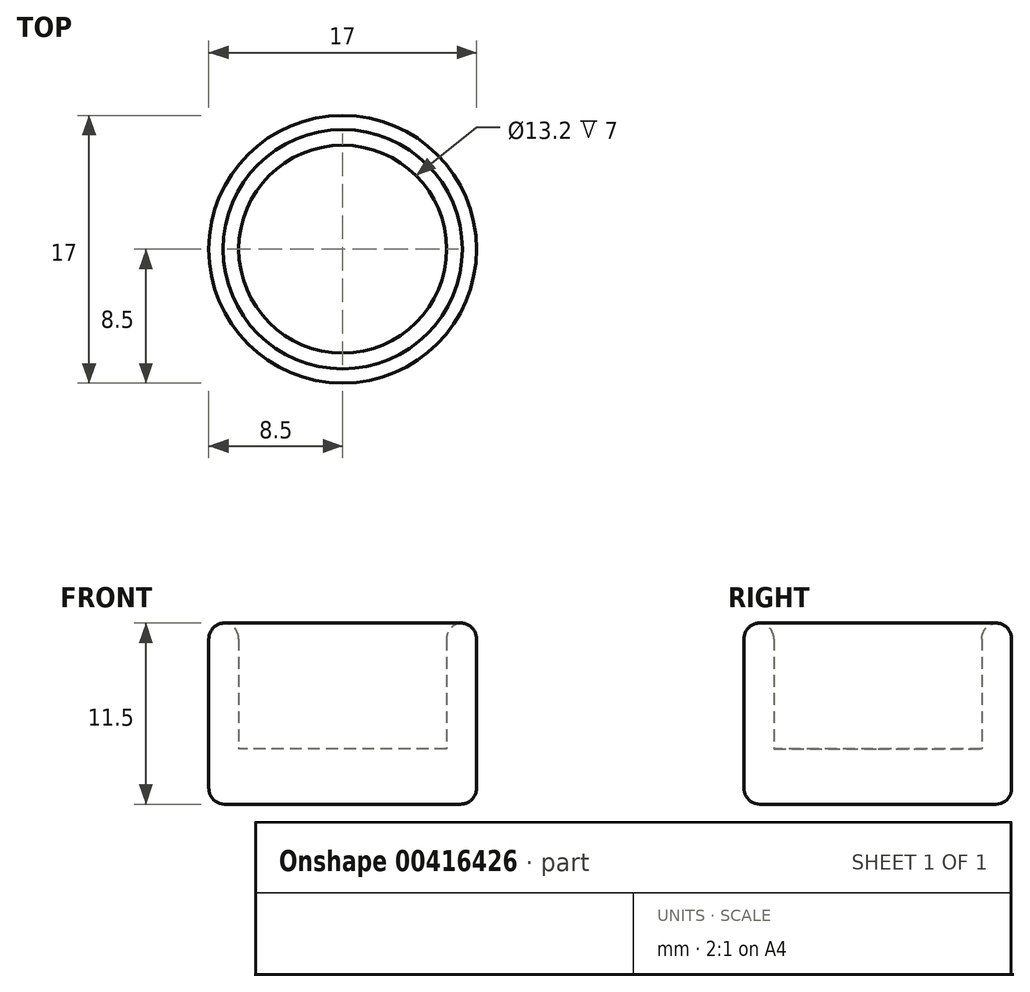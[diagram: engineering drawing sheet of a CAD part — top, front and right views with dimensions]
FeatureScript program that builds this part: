
annotation { "Feature Type Name" : "Feature", "Feature Type Description" : "" }
export const myFeature = defineFeature(function(context is Context, id is Id, definition is map)
    precondition{}
    {
        {
            var Q0;
            Q0=qCreatedBy(makeId("Top.planeOp"),FACE);
            var sketch = newSketch(context, id + "F0", { "sketchPlane" : qUnion([Q0])});
            skCircle(sketch, "E0", {"center": v(0, 0) * mm, "radius": 8.5 * mm});
            skSolve(sketch);
        }
        {
            var Q0;
            Q0=qSketchRegion(id+"F0",true);
            var Q1;
            Q1=makeQuery(id+"F0.imprint","IMPRINT",FACE,{"disambiguationData":[TD([[makeQuery(id+"F0.imprint","IMPRINT",EDGE,{"derivedFrom":sQuery(id+"F0.wireOp",EDGE,"UlGXe3JW-qBB9-Whef-HEUH-JptGj8hReMEJ")}),1.0]])]});
            extrude(context, id + "F1", {"entities" : qUnion([Q0, Q1]), "oppositeDirection" : true, "depth" : 3.5 * mm});
        }
        {
            var Q0;
            Q0=makeQuery(id+"F1.opExtrude","CAP_FACE",FACE,{"disambiguationData":[OSD([sQuery(id+"F0.wireOp",EDGE,"E0")])],"isStart":true});
            var sketch = newSketch(context, id + "F2", { "sketchPlane" : qUnion([Q0])});
            skCircle(sketch, "E1", {"center": v(0, 0) * mm, "radius": 6.6 * mm});
            skSolve(sketch);
        }
        {
            var Q0;
            Q0=makeQuery(id+"F2.imprint","IMPRINT",FACE,{"disambiguationData":[TD([[makeQuery(id+"F2.imprint","IMPRINT",EDGE,{"derivedFrom":sQuery(id+"F2.wireOp",EDGE,"E1")}),-1.0]])]});
            extrude(context, id + "F3", {"entities" : qUnion([Q0]), "operationType" : NewBodyOperationType.ADD, "depth" : 8 * mm});
        }
        {
            var Q0;
            Q0=makeQuery(id+"F3.opExtrude","CAP_EDGE",EDGE,{"disambiguationData":[OSD([sQuery(id+"F2.wireOp",EDGE,"E1")])],"isStart":false});
            var Q1;
            Q1=makeQuery(id+"F1.opExtrude","CAP_EDGE",EDGE,{"disambiguationData":[OSD([sQuery(id+"F0.wireOp",EDGE,"E0")])],"isStart":false});
            fillet(context, id + "F4", {"entities" : qUnion([Q0, Q1]), "radius" : 1 * mm, "tangentPropagation" : true, "allowEdgeOverflow" : false});
        }
        {
            var Q0;
            Q0=makeQuery(id+"F3.opExtrude","CAP_EDGE",EDGE,{"disambiguationData":[OSD([sQuery(id+"F0.wireOp",EDGE,"E0")])],"isStart":false});
            fillet(context, id + "F5", {"entities" : qUnion([Q0]), "radius" : 1 * mm, "tangentPropagation" : true, "allowEdgeOverflow" : false});
        }
    });
